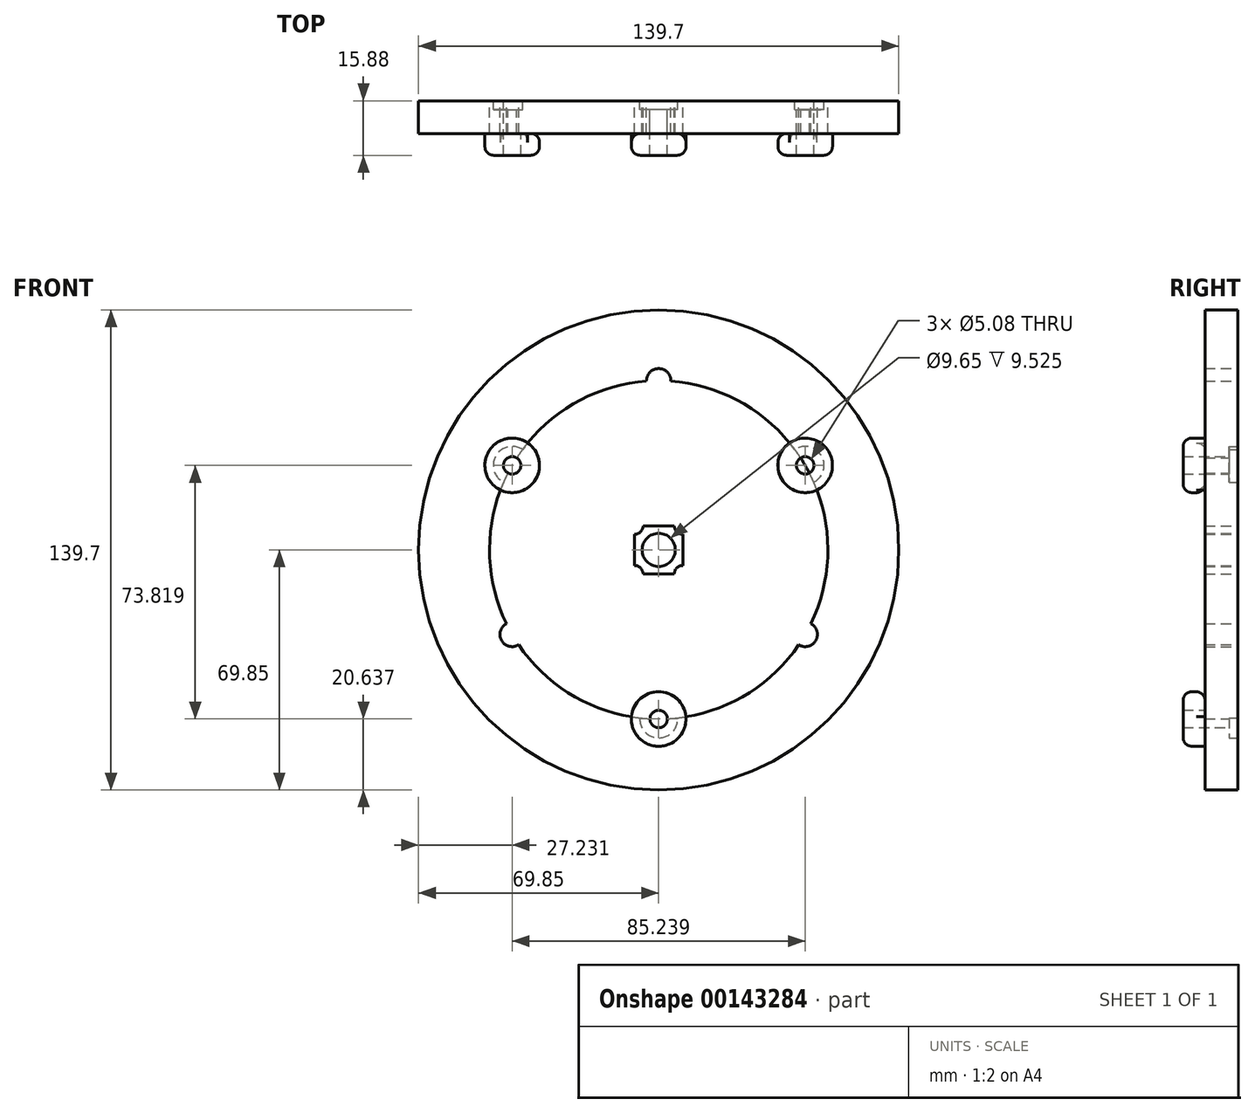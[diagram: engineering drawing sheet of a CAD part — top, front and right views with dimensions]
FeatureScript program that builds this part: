
annotation { "Feature Type Name" : "Feature", "Feature Type Description" : "" }
export const myFeature = defineFeature(function(context is Context, id is Id, definition is map)
    precondition{}
    {
        {
            var Q0;
            Q0=qCreatedBy(makeId("Front.planeOp"),FACE);
            var sketch = newSketch(context, id + "F0", { "sketchPlane" : qUnion([Q0])});
            skCircle(sketch, "E0", {"center": v(0, 0) * mm, "radius": 69.85 * mm});
            skCircle(sketch, "E1", {"center": v(0, 0) * mm, "radius": 49.21 * mm});
            skLineSegment(sketch, "E2.bottom", {"start": v(7.04, 7.04) * mm, "end": v(-7.04, 7.04) * mm});
            skLineSegment(sketch, "E2.top", {"start": v(7.04, -7.04) * mm, "end": v(-7.04, -7.04) * mm});
            skLineSegment(sketch, "E2.left", {"start": v(7.04, 7.04) * mm, "end": v(7.04, -7.04) * mm});
            skLineSegment(sketch, "E2.right", {"start": v(-7.04, 7.04) * mm, "end": v(-7.04, -7.04) * mm});
            skCircle(sketch, "E3", {"center": v(7.04, 7.04) * mm, "radius": 2.5 * mm});
            skCircle(sketch, "E4", {"center": v(7.04, -7.04) * mm, "radius": 2.5 * mm});
            skCircle(sketch, "E5", {"center": v(-7.04, -7.04) * mm, "radius": 2.5 * mm});
            skCircle(sketch, "E6", {"center": v(-7.04, 7.04) * mm, "radius": 2.5 * mm});
            skCircle(sketch, "E7", {"center": v(0, 49.21) * mm, "radius": 3.56 * mm});
            skCircle(sketch, "E8.1.0", {"center": v(-42.62, -24.6) * mm, "radius": 3.56 * mm});
            skCircle(sketch, "E8.2.0", {"center": v(42.62, -24.6) * mm, "radius": 3.56 * mm});
            skCircle(sketch, "E9", {"center": v(0, 0) * mm, "radius": 4.83 * mm});
            skCircle(sketch, "E10", {"center": v(0, -49.21) * mm, "radius": 2.54 * mm});
            skCircle(sketch, "E11.1.0", {"center": v(42.62, 24.6) * mm, "radius": 2.54 * mm});
            skCircle(sketch, "E11.2.0", {"center": v(-42.62, 24.6) * mm, "radius": 2.54 * mm});
            skSolve(sketch);
        }
        {
            var Q0;
            Q0=makeQuery(id+"F0.imprint","IMPRINT",FACE,{"disambiguationData":[TD([[makeQuery(id+"F0.imprint","IMPRINT",EDGE,{"derivedFrom":sQuery(id+"F0.wireOp",EDGE,"E0")}),1.0]])]});
            var Q1;
            {var subQ10=sQuery(id+"F0.wireOp",EDGE,"E1");var subQ17=sQuery(id+"F0.wireOp",EDGE,"E11.1.0");var subQ27=makeQuery(id+"F0.imprint","INTERSECT",VERTEX,{"disambiguationData":[OD(0.0)],"derivedFrom":[subQ10,subQ17]});Q1=makeQuery(id+"F0.imprint","IMPRINT",FACE,{"disambiguationData":[TD([[makeQuery(id+"F0.imprint","IMPRINT",EDGE,{"disambiguationData":[TD([[subQ27,-1.0]])],"derivedFrom":subQ10}),1.0]])]});}
            var Q2;
            Q2=makeQuery(id+"F0.imprint","IMPRINT",FACE,{"disambiguationData":[TD([[makeQuery(id+"F0.imprint","IMPRINT",EDGE,{"derivedFrom":sQuery(id+"F0.wireOp",EDGE,"E9")}),-1.0]])]});
            extrude(context, id + "F1", {"entities" : qUnion([Q0, Q1, Q2]), "depth" : 9.52 * mm, "offsetDistance" : 25.4 * mm});
        }
        {
            var Q0;
            Q0=makeQuery(id+"F1.opExtrude","CAP_FACE",FACE,{"disambiguationData":[OSD([sQuery(id+"F0.wireOp",EDGE,"E0"),sQuery(id+"F0.wireOp",EDGE,"E3"),sQuery(id+"F0.wireOp",EDGE,"E4"),sQuery(id+"F0.wireOp",EDGE,"E5"),sQuery(id+"F0.wireOp",EDGE,"E6"),sQuery(id+"F0.wireOp",EDGE,"E7"),sQuery(id+"F0.wireOp",EDGE,"E8.1.0"),sQuery(id+"F0.wireOp",EDGE,"E8.2.0"),sQuery(id+"F0.wireOp",EDGE,"E9"),sQuery(id+"F0.wireOp",EDGE,"E10"),sQuery(id+"F0.wireOp",EDGE,"E11.1.0"),sQuery(id+"F0.wireOp",EDGE,"E11.2.0")])],"isStart":true});
            var sketch = newSketch(context, id + "F2", { "sketchPlane" : qUnion([Q0])});
            skCircle(sketch, "E12", {"center": v(-42.62, 24.6) * mm, "radius": 5.5 * mm});
            skCircle(sketch, "E13", {"center": v(42.62, 24.6) * mm, "radius": 5.5 * mm});
            skCircle(sketch, "E14", {"center": v(0, -49.21) * mm, "radius": 5.5 * mm});
            skSolve(sketch);
        }
        {
            var Q0;
            Q0 = qSketchRegion(id + "F2", true);
            extrude(context, id + "F3", {"entities" : qUnion([Q0]), "operationType" : NewBodyOperationType.REMOVE, "oppositeDirection" : true, "depth" : 2.54 * mm, "offsetDistance" : 25.4 * mm});
        }
        {
            var Q0;
            Q0=makeQuery(id+"F1.opExtrude","CAP_FACE",FACE,{"disambiguationData":[OSD([sQuery(id+"F0.wireOp",EDGE,"E0"),sQuery(id+"F0.wireOp",EDGE,"E3"),sQuery(id+"F0.wireOp",EDGE,"E4"),sQuery(id+"F0.wireOp",EDGE,"E5"),sQuery(id+"F0.wireOp",EDGE,"E6"),sQuery(id+"F0.wireOp",EDGE,"E7"),sQuery(id+"F0.wireOp",EDGE,"E8.1.0"),sQuery(id+"F0.wireOp",EDGE,"E8.2.0"),sQuery(id+"F0.wireOp",EDGE,"E9"),sQuery(id+"F0.wireOp",EDGE,"E10"),sQuery(id+"F0.wireOp",EDGE,"E11.1.0"),sQuery(id+"F0.wireOp",EDGE,"E11.2.0")])],"isStart":false});
            var sketch = newSketch(context, id + "F4", { "sketchPlane" : qUnion([Q0])});
            skCircle(sketch, "E15", {"center": v(-42.62, 24.6) * mm, "radius": 7.94 * mm});
            skCircle(sketch, "E16", {"center": v(42.62, 24.6) * mm, "radius": 7.94 * mm});
            skCircle(sketch, "E17", {"center": v(0, -49.21) * mm, "radius": 7.94 * mm});
            skCircle(sketch, "E18", {"center": v(-42.62, 24.6) * mm, "radius": 2.54 * mm});
            skCircle(sketch, "E19", {"center": v(42.62, 24.6) * mm, "radius": 2.54 * mm});
            skCircle(sketch, "E20", {"center": v(0, -49.21) * mm, "radius": 2.54 * mm});
            skSolve(sketch);
        }
        {
            var Q0;
            Q0 = qSketchRegion(id + "F4", true);
            extrude(context, id + "F5", {"entities" : qUnion([Q0]), "operationType" : NewBodyOperationType.ADD, "depth" : 6.35 * mm, "offsetDistance" : 25.4 * mm});
        }
        {
            var Q0;
            Q0=makeQuery(id+"F5.opExtrude","CAP_EDGE",EDGE,{"disambiguationData":[OSD([sQuery(id+"F4.wireOp",EDGE,"E15")])],"isStart":false});
            var Q1;
            Q1=makeQuery(id+"F5.opExtrude","CAP_EDGE",EDGE,{"disambiguationData":[OSD([sQuery(id+"F4.wireOp",EDGE,"E17")])],"isStart":false});
            var Q2;
            Q2=makeQuery(id+"F5.opExtrude","CAP_EDGE",EDGE,{"disambiguationData":[OSD([sQuery(id+"F4.wireOp",EDGE,"E16")])],"isStart":false});
            var Q3;
            Q3=makeQuery(id+"F5.opExtrude","CAP_EDGE",EDGE,{"disambiguationData":[OSD([sQuery(id+"F4.wireOp",EDGE,"E15")])],"isStart":true});
            var Q4;
            Q4=makeQuery(id+"F5.opExtrude","CAP_EDGE",EDGE,{"disambiguationData":[OSD([sQuery(id+"F4.wireOp",EDGE,"E17")])],"isStart":true});
            var Q5;
            Q5=makeQuery(id+"F5.opExtrude","CAP_EDGE",EDGE,{"disambiguationData":[OSD([sQuery(id+"F4.wireOp",EDGE,"E16")])],"isStart":true});
            fillet(context, id + "F6", {"entities" : qUnion([Q0, Q1, Q2, Q3, Q4, Q5]), "radius" : 2.54 * mm, "tangentPropagation" : true, "allowEdgeOverflow" : false});
        }
    });
